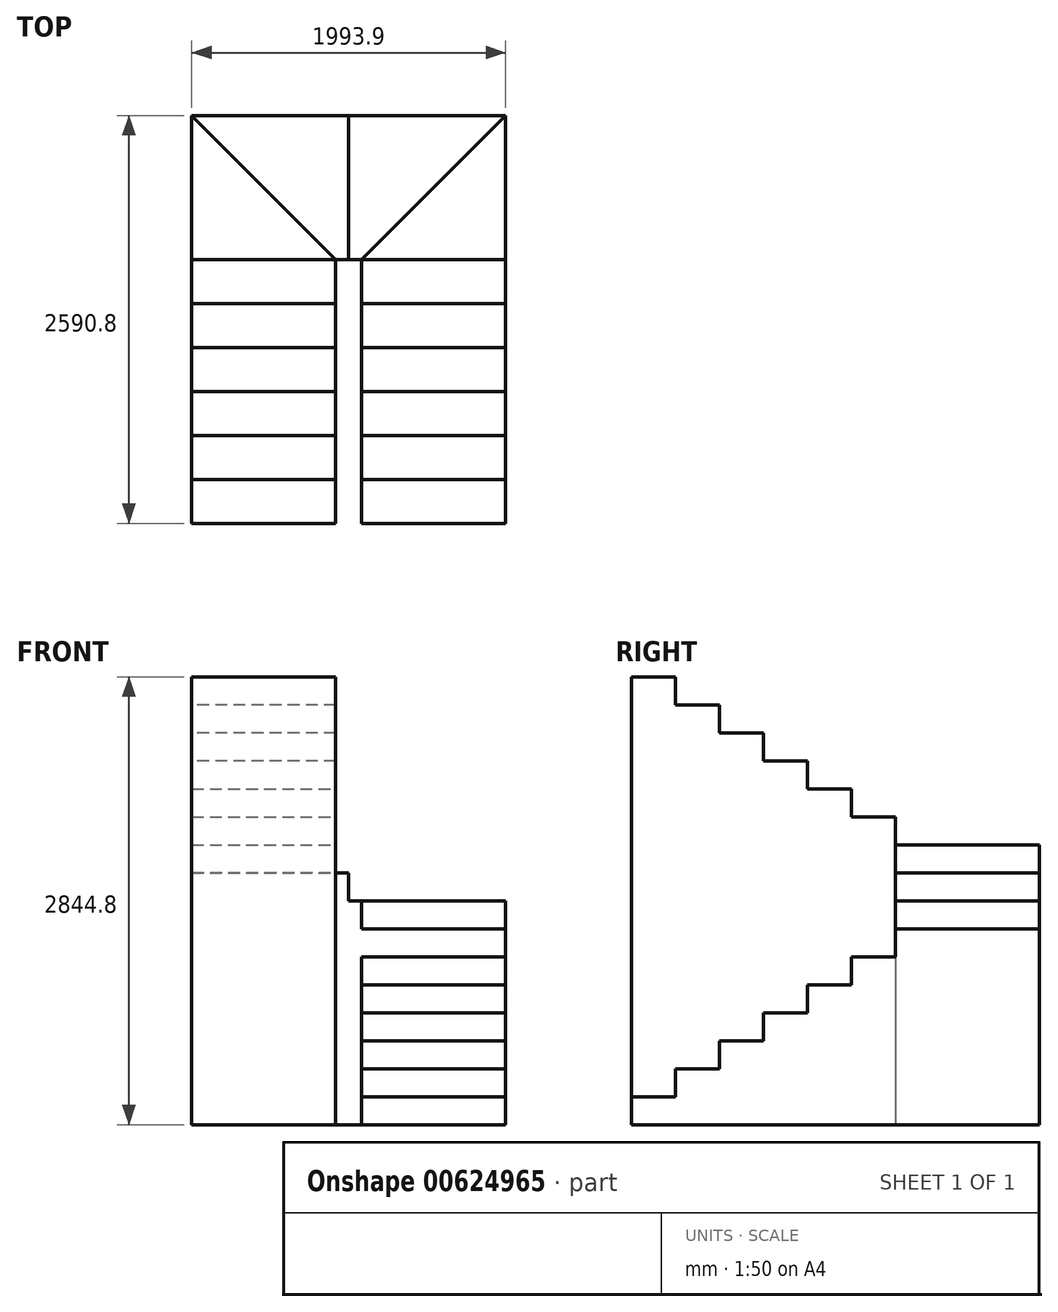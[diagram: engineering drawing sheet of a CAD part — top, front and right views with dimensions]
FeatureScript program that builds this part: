
annotation { "Feature Type Name" : "Feature", "Feature Type Description" : "" }
export const myFeature = defineFeature(function(context is Context, id is Id, definition is map)
    precondition{}
    {
        {
            var Q0;
            Q0=qCreatedBy(makeId("Top.planeOp"),FACE);
            var sketch = newSketch(context, id + "F0", { "sketchPlane" : qUnion([Q0])});
            skLineSegment(sketch, "E0.bottom", {"start": v(0, 0) * mm, "end": v(165.1, 0) * mm});
            skLineSegment(sketch, "E0.left", {"start": v(0, 0) * mm, "end": v(0, -1397) * mm});
            skLineSegment(sketch, "E0.right", {"start": v(165.1, 0) * mm, "end": v(165.1, -1397) * mm});
            skLineSegment(sketch, "E1", {"start": v(82.55, 0) * mm, "end": v(82.55, 914.4) * mm});
            skLineSegment(sketch, "E2", {"start": v(82.55, 914.4) * mm, "end": v(1079.5, 914.4) * mm});
            skLineSegment(sketch, "E3", {"start": v(1079.5, 914.4) * mm, "end": v(165.1, 0) * mm});
            skLineSegment(sketch, "E4", {"start": v(165.1, 0) * mm, "end": v(1079.5, 0) * mm});
            skLineSegment(sketch, "E5", {"start": v(1079.5, 0) * mm, "end": v(1079.5, 914.4) * mm});
            skLineSegment(sketch, "E6", {"start": v(1079.5, 0) * mm, "end": v(1079.5, -1397) * mm});
            skLineSegment(sketch, "E7", {"start": v(1079.5, -1397) * mm, "end": v(165.1, -1397) * mm});
            skLineSegment(sketch, "E8", {"start": v(165.1, -279.4) * mm, "end": v(1079.5, -279.4) * mm});
            skLineSegment(sketch, "E9", {"start": v(165.1, -838.2) * mm, "end": v(1079.5, -838.2) * mm});
            skLineSegment(sketch, "E10", {"start": v(165.1, -1117.6) * mm, "end": v(1079.5, -1117.6) * mm});
            skLineSegment(sketch, "E11", {"start": v(165.1, -558.8) * mm, "end": v(1079.5, -558.8) * mm});
            skLineSegment(sketch, "E12", {"start": v(82.55, 914.4) * mm, "end": v(-914.4, 914.4) * mm});
            skLineSegment(sketch, "E13", {"start": v(-914.4, 914.4) * mm, "end": v(0, 0) * mm});
            skLineSegment(sketch, "E14", {"start": v(-914.4, 914.4) * mm, "end": v(-914.4, 0) * mm});
            skLineSegment(sketch, "E15", {"start": v(-914.4, 0) * mm, "end": v(0, 0) * mm});
            skLineSegment(sketch, "E16", {"start": v(-914.4, 0) * mm, "end": v(-914.4, -279.4) * mm});
            skLineSegment(sketch, "E17", {"start": v(-914.4, -279.4) * mm, "end": v(0, -279.4) * mm});
            skLineSegment(sketch, "E18", {"start": v(0, -558.8) * mm, "end": v(-914.4, -558.8) * mm});
            skLineSegment(sketch, "E19", {"start": v(-914.4, -558.8) * mm, "end": v(-914.4, -279.4) * mm});
            skLineSegment(sketch, "E20", {"start": v(0, -838.2) * mm, "end": v(-914.4, -838.2) * mm});
            skLineSegment(sketch, "E21", {"start": v(-914.4, -838.2) * mm, "end": v(-914.4, -558.8) * mm});
            skLineSegment(sketch, "E22", {"start": v(0, -1117.6) * mm, "end": v(-914.4, -1117.6) * mm});
            skLineSegment(sketch, "E23", {"start": v(-914.4, -1117.6) * mm, "end": v(-914.4, -838.2) * mm});
            skLineSegment(sketch, "E24", {"start": v(0, -1397) * mm, "end": v(-914.4, -1397) * mm});
            skLineSegment(sketch, "E25", {"start": v(-914.4, -1397) * mm, "end": v(-914.4, -1117.6) * mm});
            skLineSegment(sketch, "E26", {"start": v(165.1, -1397) * mm, "end": v(165.1, -1676.4) * mm});
            skLineSegment(sketch, "E27", {"start": v(165.1, -1676.4) * mm, "end": v(1079.5, -1676.4) * mm});
            skLineSegment(sketch, "E28", {"start": v(1079.5, -1676.4) * mm, "end": v(1079.5, -1397) * mm});
            skLineSegment(sketch, "E29", {"start": v(-914.4, -1397) * mm, "end": v(-914.4, -1676.4) * mm});
            skLineSegment(sketch, "E30", {"start": v(-914.4, -1676.4) * mm, "end": v(0, -1676.4) * mm});
            skLineSegment(sketch, "E31", {"start": v(0, -1676.4) * mm, "end": v(0, -1397) * mm});
            skSolve(sketch);
        }
        {
            var Q0;
            Q0=makeQuery(id+"F0.imprint","IMPRINT",FACE,{"disambiguationData":[TD([[makeQuery(id+"F0.imprint","IMPRINT",EDGE,{"derivedFrom":sQuery(id+"F0.wireOp",EDGE,"E7")}),1.0]])]});
            extrude(context, id + "F1", {"entities" : qUnion([Q0]), "depth" : 177.8 * mm, "offsetDistance" : 25.4 * mm});
        }
        {
            var Q0;
            {var subQ0=sQuery(id+"F0.wireOp",EDGE,"E7");Q0=makeQuery(id+"F0.imprint","IMPRINT",FACE,{"disambiguationData":[TD([[makeQuery(id+"F0.imprint","IMPRINT",EDGE,{"derivedFrom":subQ0}),-1.0]])]});}
            extrude(context, id + "F2", {"entities" : qUnion([Q0]), "operationType" : NewBodyOperationType.ADD, "depth" : 355.6 * mm, "offsetDistance" : 25.4 * mm});
        }
        {
            var Q0;
            {var subQ0=sQuery(id+"F0.wireOp",EDGE,"E9");Q0=makeQuery(id+"F0.imprint","IMPRINT",FACE,{"disambiguationData":[TD([[makeQuery(id+"F0.imprint","IMPRINT",EDGE,{"derivedFrom":subQ0}),-1.0]])]});}
            extrude(context, id + "F3", {"entities" : qUnion([Q0]), "operationType" : NewBodyOperationType.ADD, "depth" : 533.4 * mm, "offsetDistance" : 25.4 * mm});
        }
        {
            var Q0;
            {var subQ0=sQuery(id+"F0.wireOp",EDGE,"E9");Q0=makeQuery(id+"F0.imprint","IMPRINT",FACE,{"disambiguationData":[TD([[makeQuery(id+"F0.imprint","IMPRINT",EDGE,{"derivedFrom":subQ0}),1.0]])]});}
            extrude(context, id + "F4", {"entities" : qUnion([Q0]), "operationType" : NewBodyOperationType.ADD, "depth" : 711.2 * mm, "offsetDistance" : 25.4 * mm});
        }
        {
            var Q0;
            {var subQ0=sQuery(id+"F0.wireOp",EDGE,"E8");Q0=makeQuery(id+"F0.imprint","IMPRINT",FACE,{"disambiguationData":[TD([[makeQuery(id+"F0.imprint","IMPRINT",EDGE,{"derivedFrom":subQ0}),-1.0]])]});}
            extrude(context, id + "F5", {"entities" : qUnion([Q0]), "operationType" : NewBodyOperationType.ADD, "depth" : 889 * mm, "offsetDistance" : 25.4 * mm});
        }
        {
            var Q0;
            {var subQ0=sQuery(id+"F0.wireOp",EDGE,"E4");Q0=makeQuery(id+"F0.imprint","IMPRINT",FACE,{"disambiguationData":[TD([[makeQuery(id+"F0.imprint","IMPRINT",EDGE,{"derivedFrom":subQ0}),-1.0]])]});}
            extrude(context, id + "F6", {"entities" : qUnion([Q0]), "operationType" : NewBodyOperationType.ADD, "depth" : 1066.8 * mm, "offsetDistance" : 25.4 * mm});
        }
        {
            var Q0;
            Q0=makeQuery(id+"F0.imprint","IMPRINT",FACE,{"disambiguationData":[TD([[makeQuery(id+"F0.imprint","IMPRINT",EDGE,{"derivedFrom":sQuery(id+"F0.wireOp",EDGE,"E3")}),1.0]])]});
            extrude(context, id + "F7", {"entities" : qUnion([Q0]), "operationType" : NewBodyOperationType.ADD, "depth" : 1244.6 * mm, "offsetDistance" : 25.4 * mm});
        }
        {
            var Q0;
            {var subQ2=sQuery(id+"F0.wireOp",EDGE,"E1");Q0=makeQuery(id+"F0.imprint","IMPRINT",FACE,{"disambiguationData":[TD([[makeQuery(id+"F0.imprint","IMPRINT",EDGE,{"derivedFrom":subQ2}),-1.0]])]});}
            extrude(context, id + "F8", {"entities" : qUnion([Q0]), "operationType" : NewBodyOperationType.ADD, "depth" : 1422.4 * mm, "offsetDistance" : 25.4 * mm});
        }
        {
            var Q0;
            {var subQ2=sQuery(id+"F0.wireOp",EDGE,"E1");Q0=makeQuery(id+"F0.imprint","IMPRINT",FACE,{"disambiguationData":[TD([[makeQuery(id+"F0.imprint","IMPRINT",EDGE,{"derivedFrom":subQ2}),1.0]])]});}
            extrude(context, id + "F9", {"entities" : qUnion([Q0]), "operationType" : NewBodyOperationType.ADD, "depth" : 1600.2 * mm, "offsetDistance" : 25.4 * mm});
        }
        {
            var Q0;
            Q0=makeQuery(id+"F0.imprint","IMPRINT",FACE,{"disambiguationData":[TD([[makeQuery(id+"F0.imprint","IMPRINT",EDGE,{"derivedFrom":sQuery(id+"F0.wireOp",EDGE,"E13")}),-1.0]])]});
            extrude(context, id + "F10", {"entities" : qUnion([Q0]), "operationType" : NewBodyOperationType.ADD, "depth" : 1778 * mm, "offsetDistance" : 25.4 * mm});
        }
        {
            var Q0;
            {var subQ0=sQuery(id+"F0.wireOp",EDGE,"E15");Q0=makeQuery(id+"F0.imprint","IMPRINT",FACE,{"disambiguationData":[TD([[makeQuery(id+"F0.imprint","IMPRINT",EDGE,{"derivedFrom":subQ0}),-1.0]])]});}
            extrude(context, id + "F11", {"entities" : qUnion([Q0]), "operationType" : NewBodyOperationType.ADD, "depth" : 1955.8 * mm, "offsetDistance" : 25.4 * mm});
        }
        {
            var Q0;
            {var subQ0=sQuery(id+"F0.wireOp",EDGE,"E17");Q0=makeQuery(id+"F0.imprint","IMPRINT",FACE,{"disambiguationData":[TD([[makeQuery(id+"F0.imprint","IMPRINT",EDGE,{"derivedFrom":subQ0}),-1.0]])]});}
            extrude(context, id + "F12", {"entities" : qUnion([Q0]), "operationType" : NewBodyOperationType.ADD, "depth" : 2133.6 * mm, "offsetDistance" : 25.4 * mm});
        }
        {
            var Q0;
            {var subQ0=sQuery(id+"F0.wireOp",EDGE,"E18");Q0=makeQuery(id+"F0.imprint","IMPRINT",FACE,{"disambiguationData":[TD([[makeQuery(id+"F0.imprint","IMPRINT",EDGE,{"derivedFrom":subQ0}),1.0]])]});}
            extrude(context, id + "F13", {"entities" : qUnion([Q0]), "operationType" : NewBodyOperationType.ADD, "depth" : 2311.4 * mm, "offsetDistance" : 25.4 * mm});
        }
        {
            var Q0;
            {var subQ0=sQuery(id+"F0.wireOp",EDGE,"E20");Q0=makeQuery(id+"F0.imprint","IMPRINT",FACE,{"disambiguationData":[TD([[makeQuery(id+"F0.imprint","IMPRINT",EDGE,{"derivedFrom":subQ0}),1.0]])]});}
            extrude(context, id + "F14", {"entities" : qUnion([Q0]), "operationType" : NewBodyOperationType.ADD, "depth" : 2489.2 * mm, "offsetDistance" : 25.4 * mm});
        }
        {
            var Q0;
            {var subQ2=sQuery(id+"F0.wireOp",EDGE,"E22");Q0=makeQuery(id+"F0.imprint","IMPRINT",FACE,{"disambiguationData":[TD([[makeQuery(id+"F0.imprint","IMPRINT",EDGE,{"derivedFrom":subQ2}),1.0]])]});}
            extrude(context, id + "F15", {"entities" : qUnion([Q0]), "operationType" : NewBodyOperationType.ADD, "depth" : 2667 * mm, "offsetDistance" : 25.4 * mm});
        }
        {
            var Q0;
            Q0=makeQuery(id+"F0.imprint","IMPRINT",FACE,{"disambiguationData":[TD([[makeQuery(id+"F0.imprint","IMPRINT",EDGE,{"derivedFrom":sQuery(id+"F0.wireOp",EDGE,"E24")}),1.0]])]});
            extrude(context, id + "F16", {"entities" : qUnion([Q0]), "operationType" : NewBodyOperationType.ADD, "depth" : 2844.8 * mm, "offsetDistance" : 25.4 * mm});
        }
    });
